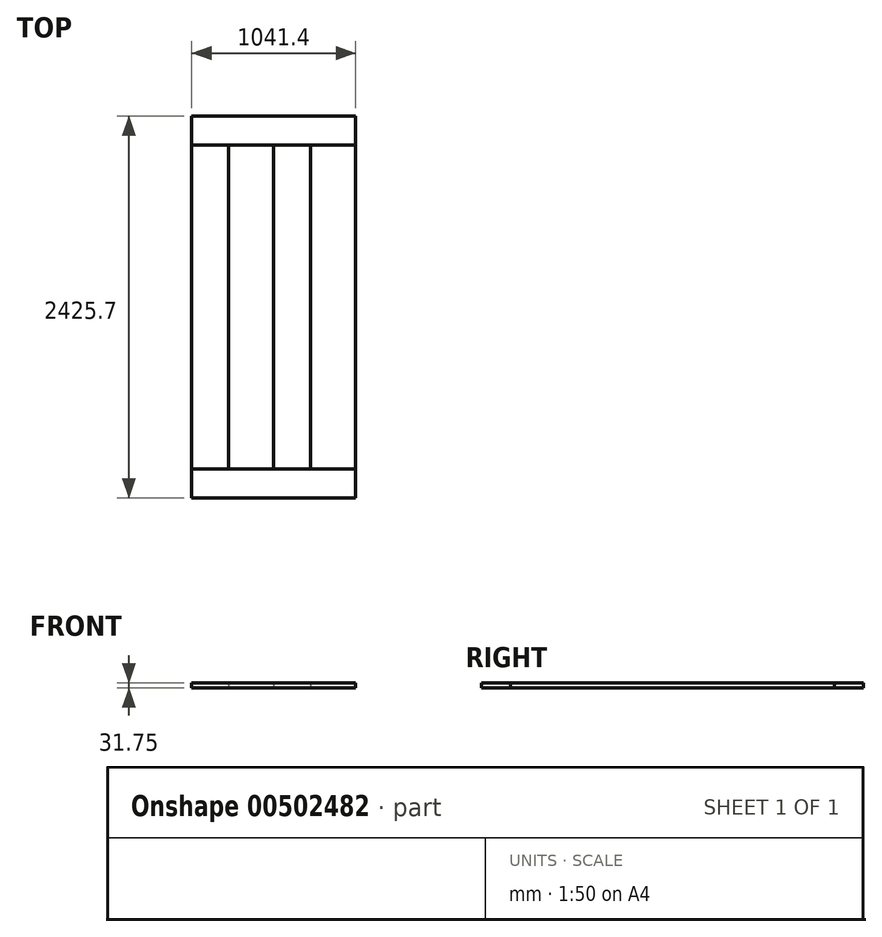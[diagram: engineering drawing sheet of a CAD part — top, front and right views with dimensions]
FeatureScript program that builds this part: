
annotation { "Feature Type Name" : "Feature", "Feature Type Description" : "" }
export const myFeature = defineFeature(function(context is Context, id is Id, definition is map)
    precondition{}
    {
        {
            var Q0;
            Q0=qCreatedBy(makeId("Top.planeOp"),FACE);
            var sketch = newSketch(context, id + "F0", { "sketchPlane" : qUnion([Q0])});
            skLineSegment(sketch, "E0.bottom", {"start": v(0, -1028.7) * mm, "end": v(-285.75, -1028.7) * mm});
            skLineSegment(sketch, "E0.top", {"start": v(0, 1028.7) * mm, "end": v(-285.75, 1028.7) * mm});
            skLineSegment(sketch, "E0.left", {"start": v(0, -1028.7) * mm, "end": v(0, 1028.7) * mm});
            skLineSegment(sketch, "E0.right", {"start": v(-285.75, -1028.7) * mm, "end": v(-285.75, 1028.7) * mm});
            skPoint(sketch, "E0.middle", {"position": v(-142.87, 0) * mm});
            skSolve(sketch);
        }
        {
            var Q0;
            Q0=qCreatedBy(makeId("Top.planeOp"),FACE);
            var sketch = newSketch(context, id + "F1", { "sketchPlane" : qUnion([Q0])});
            skLineSegment(sketch, "E1.bottom", {"start": v(0, 1028.7) * mm, "end": v(234.95, 1028.7) * mm});
            skLineSegment(sketch, "E1.top", {"start": v(0, -1028.7) * mm, "end": v(234.95, -1028.7) * mm});
            skLineSegment(sketch, "E1.left", {"start": v(0, 1028.7) * mm, "end": v(0, -1028.7) * mm});
            skLineSegment(sketch, "E1.right", {"start": v(234.95, 1028.7) * mm, "end": v(234.95, -1028.7) * mm});
            skSolve(sketch);
        }
        {
            var Q0;
            Q0=qCreatedBy(makeId("Top.planeOp"),FACE);
            var sketch = newSketch(context, id + "F2", { "sketchPlane" : qUnion([Q0])});
            skLineSegment(sketch, "E2.bottom", {"start": v(234.95, 1028.7) * mm, "end": v(520.7, 1028.7) * mm});
            skLineSegment(sketch, "E2.top", {"start": v(234.95, -1028.7) * mm, "end": v(520.7, -1028.7) * mm});
            skLineSegment(sketch, "E2.left", {"start": v(234.95, 1028.7) * mm, "end": v(234.95, -1028.7) * mm});
            skLineSegment(sketch, "E2.right", {"start": v(520.7, 1028.7) * mm, "end": v(520.7, -1028.7) * mm});
            skSolve(sketch);
        }
        {
            var Q0;
            Q0=qCreatedBy(makeId("Top.planeOp"),FACE);
            var sketch = newSketch(context, id + "F3", { "sketchPlane" : qUnion([Q0])});
            skLineSegment(sketch, "E3.bottom", {"start": v(-520.7, 1028.7) * mm, "end": v(-285.75, 1028.7) * mm});
            skLineSegment(sketch, "E3.top", {"start": v(-520.7, -1028.7) * mm, "end": v(-285.75, -1028.7) * mm});
            skLineSegment(sketch, "E3.left", {"start": v(-520.7, 1028.7) * mm, "end": v(-520.7, -1028.7) * mm});
            skLineSegment(sketch, "E3.right", {"start": v(-285.75, 1028.7) * mm, "end": v(-285.75, -1028.7) * mm});
            skSolve(sketch);
        }
        {
            var Q0;
            Q0=qCreatedBy(makeId("Top.planeOp"),FACE);
            var sketch = newSketch(context, id + "F4", { "sketchPlane" : qUnion([Q0])});
            skLineSegment(sketch, "E4.bottom", {"start": v(-520.7, 1212.85) * mm, "end": v(520.7, 1212.85) * mm});
            skLineSegment(sketch, "E4.top", {"start": v(-520.7, 1028.7) * mm, "end": v(520.7, 1028.7) * mm});
            skLineSegment(sketch, "E4.left", {"start": v(-520.7, 1212.85) * mm, "end": v(-520.7, 1028.7) * mm});
            skLineSegment(sketch, "E4.right", {"start": v(520.7, 1212.85) * mm, "end": v(520.7, 1028.7) * mm});
            skLineSegment(sketch, "E5.bottom", {"start": v(-520.7, -1028.7) * mm, "end": v(520.7, -1028.7) * mm});
            skLineSegment(sketch, "E5.top", {"start": v(-520.7, -1212.85) * mm, "end": v(520.7, -1212.85) * mm});
            skLineSegment(sketch, "E5.left", {"start": v(-520.7, -1028.7) * mm, "end": v(-520.7, -1212.85) * mm});
            skLineSegment(sketch, "E5.right", {"start": v(520.7, -1028.7) * mm, "end": v(520.7, -1212.85) * mm});
            skSolve(sketch);
        }
        {
            var Q0;
            Q0 = qSketchRegion(id + "F0", true);
            var Q1;
            Q1 = qSketchRegion(id + "F1", true);
            var Q2;
            Q2 = qSketchRegion(id + "F2", true);
            var Q3;
            Q3 = qSketchRegion(id + "F3", true);
            var Q4;
            Q4 = qSketchRegion(id + "F4", true);
            extrude(context, id + "F5", {"entities" : qUnion([Q0, Q1, Q2, Q3, Q4]), "depth" : 31.75 * mm});
        }
    });
